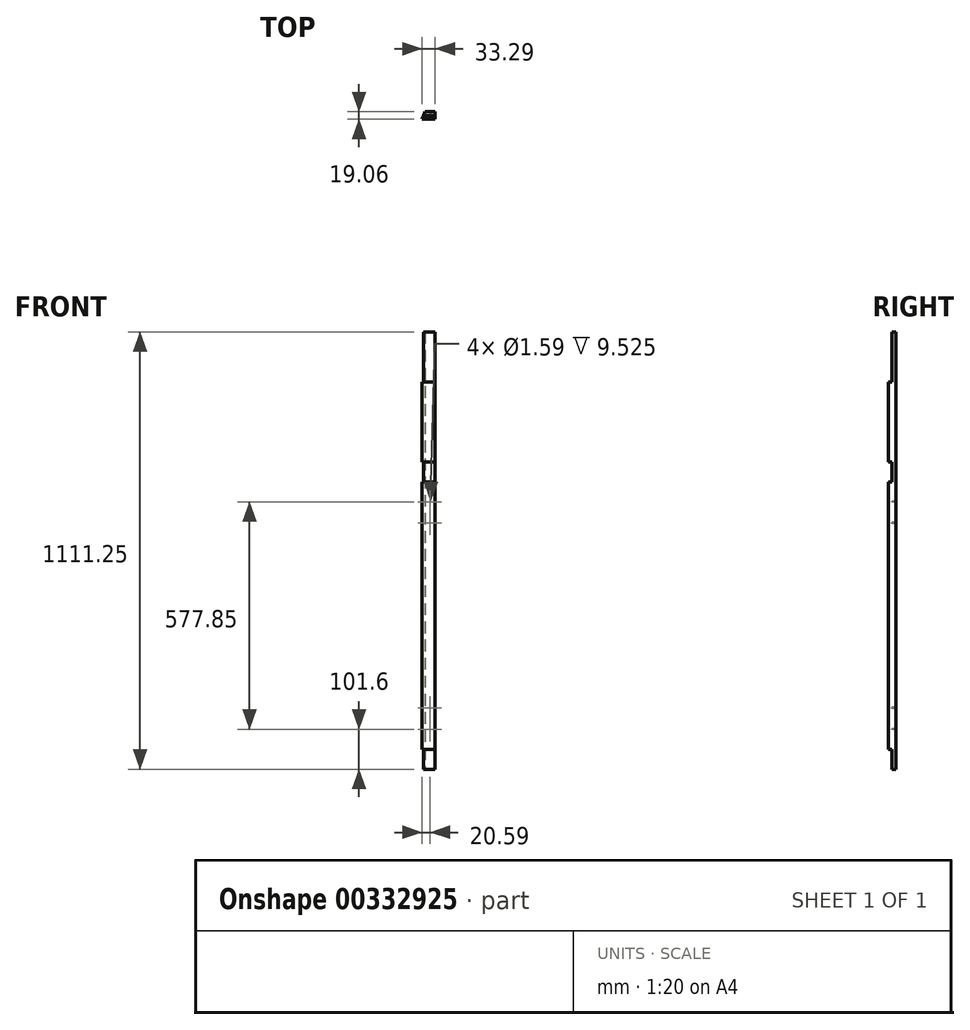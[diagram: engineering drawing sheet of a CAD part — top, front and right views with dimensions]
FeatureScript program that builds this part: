
annotation { "Feature Type Name" : "Feature", "Feature Type Description" : "" }
export const myFeature = defineFeature(function(context is Context, id is Id, definition is map)
    precondition{}
    {
        {
            var Q0;
            Q0=qCreatedBy(makeId("Top.planeOp"),FACE);
            var sketch = newSketch(context, id + "F0", { "sketchPlane" : qUnion([Q0])});
            skLineSegment(sketch, "E0.bottom", {"start": v(25.4, 9.53) * mm, "end": v(0, 9.53) * mm});
            skLineSegment(sketch, "E0.top", {"start": v(25.4, -9.53) * mm, "end": v(-7.9, -9.53) * mm});
            skLineSegment(sketch, "E0.left", {"start": v(25.4, 9.53) * mm, "end": v(25.4, -9.52) * mm});
            skPoint(sketch, "E0.middle", {"position": v(0, 0) * mm});
            skLineSegment(sketch, "E1", {"start": v(0, 9.53) * mm, "end": v(-7.9, -9.52) * mm});
            skPoint(sketch, "E0.right.end.orphan", {"position": v(-25.4, -9.53) * mm});
            skPoint(sketch, "E2.orphan", {"position": v(-25.4, 9.53) * mm});
            skSolve(sketch);
        }
        {
            var Q0;
            Q0=makeQuery(id+"F0.imprint","IMPRINT",FACE,{"disambiguationData":[TD([[makeQuery(id+"F0.imprint","IMPRINT",EDGE,{"derivedFrom":sQuery(id+"F0.wireOp",EDGE,"E0.bottom")}),1.0]])]});
            extrude(context, id + "F1", {"entities" : qUnion([Q0]), "depth" : 1111.25 * mm});
        }
        {
            var Q0;
            Q0=qCreatedBy(makeId("Front.planeOp"),FACE);
            var sketch = newSketch(context, id + "F2", { "sketchPlane" : qUnion([Q0])});
            skLineSegment(sketch, "E3.bottom", {"start": v(-38.77, 0) * mm, "end": v(83.66, 0) * mm});
            skLineSegment(sketch, "E3.top", {"start": v(-38.77, 50.8) * mm, "end": v(83.66, 50.8) * mm});
            skLineSegment(sketch, "E3.left", {"start": v(-38.77, 0) * mm, "end": v(-38.77, 50.8) * mm});
            skLineSegment(sketch, "E3.right", {"start": v(83.66, 0) * mm, "end": v(83.66, 50.8) * mm});
            skLineSegment(sketch, "E4.bottom", {"start": v(-44.21, 730.25) * mm, "end": v(49.65, 730.25) * mm});
            skLineSegment(sketch, "E4.top", {"start": v(-44.21, 781.05) * mm, "end": v(49.65, 781.05) * mm});
            skLineSegment(sketch, "E4.left", {"start": v(-44.21, 730.25) * mm, "end": v(-44.21, 781.05) * mm});
            skLineSegment(sketch, "E4.right", {"start": v(49.65, 730.25) * mm, "end": v(49.65, 781.05) * mm});
            skLineSegment(sketch, "E5.bottom", {"start": v(-210.36, 984.25) * mm, "end": v(132.8, 984.25) * mm});
            skLineSegment(sketch, "E5.top", {"start": v(-210.36, 1111.25) * mm, "end": v(132.8, 1111.25) * mm});
            skLineSegment(sketch, "E5.left", {"start": v(-210.36, 984.25) * mm, "end": v(-210.36, 1111.25) * mm});
            skLineSegment(sketch, "E5.right", {"start": v(132.8, 984.25) * mm, "end": v(132.8, 1111.25) * mm});
            skSolve(sketch);
        }
        {
            var Q0;
            Q0=qSketchRegion(id+"F2",true);
            extrude(context, id + "F3", {"entities" : qUnion([Q0]), "operationType" : NewBodyOperationType.REMOVE, "depth" : 25.4 * mm});
        }
        {
            var Q0;
            Q0=qCreatedBy(makeId("Front.planeOp"),FACE);
            var sketch = newSketch(context, id + "F4", { "sketchPlane" : qUnion([Q0])});
            skCircle(sketch, "E6", {"center": v(12.7, 101.6) * mm, "radius": 0.8 * mm});
            skCircle(sketch, "E7", {"center": v(12.7, 155.58) * mm, "radius": 0.8 * mm});
            skCircle(sketch, "E8", {"center": v(12.7, 625.48) * mm, "radius": 0.8 * mm});
            skCircle(sketch, "E9", {"center": v(12.7, 679.45) * mm, "radius": 0.8 * mm});
            skLineSegment(sketch, "E10", {"start": v(0, 0) * mm, "end": v(0, 1192.46) * mm, "construction": true});
            skLineSegment(sketch, "E11.bottom", {"start": v(12.7, 101.6) * mm, "end": v(-12.7, 101.6) * mm, "construction": true});
            skLineSegment(sketch, "E11.top", {"start": v(12.7, 679.45) * mm, "end": v(-12.7, 679.45) * mm, "construction": true});
            skLineSegment(sketch, "E11.left", {"start": v(12.7, 101.6) * mm, "end": v(12.7, 679.45) * mm, "construction": true});
            skLineSegment(sketch, "E11.right", {"start": v(-12.7, 101.6) * mm, "end": v(-12.7, 679.45) * mm, "construction": true});
            skCircle(sketch, "E12", {"center": v(-12.7, 625.48) * mm, "radius": 0.8 * mm});
            skCircle(sketch, "E13", {"center": v(-12.7, 679.45) * mm, "radius": 0.8 * mm});
            skCircle(sketch, "E14", {"center": v(-12.7, 101.6) * mm, "radius": 0.8 * mm});
            skCircle(sketch, "E15", {"center": v(-12.7, 155.58) * mm, "radius": 0.8 * mm});
            skSolve(sketch);
        }
        {
            var Q0;
            Q0=qSketchRegion(id+"F4",true);
            extrude(context, id + "F5", {"entities" : qUnion([Q0]), "operationType" : NewBodyOperationType.REMOVE, "oppositeDirection" : true, "depth" : 25.4 * mm});
        }
    });
